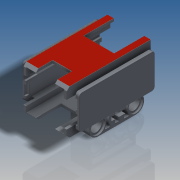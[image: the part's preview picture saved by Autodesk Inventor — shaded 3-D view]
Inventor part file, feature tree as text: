
AUTODESK INVENTOR PART (.ipt)
format: ipt  version: 2016 SP2 (Build 200236200, 236)  size: 774,656 bytes
history: native  units: in
note: dims shown in document units (in); Inventor stores cm internally (conversion verified against a paired STEP export)
features: extrude x13, sketch x3, projected_geometry x2, mirror x1, fillet x1
ambient origin geometry x8: Origin, YZ Plane, XZ Plane, XY Plane, X Axis, Y Axis, Z Axis, Center Point
bodies: Solid1 (feature_tree)
feature tree (20):
  sketch  "Sketch2"  dims[d0=0.0472in d1=1.4016in]
  extrude  "Extrusion1"  Depth=0.0472in
  extrude  "Extrusion2"  Depth=0.1732in
  extrude  "Extrusion3"  Depth=0.2835in
  extrude  "Extrusion4"  Depth=0.0157in
  extrude  "Extrusion6"  Depth=0.4252in
  extrude  "Extrusion7"  Depth=0.0157in
  extrude  "Extrusion8"  Depth=0.0157in TaperAngle=0.0deg
  extrude  "Extrusion9"  Depth=0.6299in
  extrude  "Extrusion10"  TaperAngle=0.0deg  [1 undecoded]
  extrude  "Extrusion11"  Depth=0.315in
  extrude  "Extrusion12"  TaperAngle=0.0deg  [1 undecoded]
  sketch  "Sketch4"  dims[d4=0.1417in d5=0.2835in d6=0.5039in d7=0.4252in d8=0.7244in d9=0.7244in d10=0.0in d11=0.6299in d12=0.0in d13=0.315in d14=0.0in d15=0.5039in d16=0.0in d19=0.315in d20=0.189in d21=0.2441in d22=45.0deg d23=0.2835in d24=0.2835in d25=0.0472in d26=0.063in d27=0.6772in d28=0.0787in d29=0.0472in d30=0.315in d31=0.0472in d32=0.0472in d33=0.1732in d34=0.126in d35=0.189in d36=0.0in d37=0.063in d38=0.0in d39=0.252in d40=0.0in d41=0.315in d42=0.0in d43=0.189in d44=0.0in d45=0.0472in d46=0.063in d47=0.0in d49=0.0472in d50=1.0709in d51=0.1417in d52=0.0472in d53=0.0in d54=0.0472in d55=0.5669in d56=1.2598in d57=0.0472in d58=0.1575in d59=0.7087in d60=0.2677in d61=0.1575in d62=0.0472in d63=0.0472in d64=0.063in d65=0.0in d66=0.0315in d67=0.0in d68=0.0039in d69=0.0157in]
  extrude  "Extrusion13"  Depth=0.0157in TaperAngle=0.0deg
  extrude  "Extrusion14"  Depth=0.315in
  mirror  "Mirror1"
  fillet  "Fillet1"  Radius=0.189in
  sketch  "Sketch3"  dims[d2=0.1732in d3=0.7402in]
  projected_geometry  "Projected Loop1"
  projected_geometry  "Projected Loop2"
note: 2 required parameter values undecoded (feature->parameter linkage not recoverable at this tier; creation-order binding heuristic only, values carry confidence <= 0.55)
